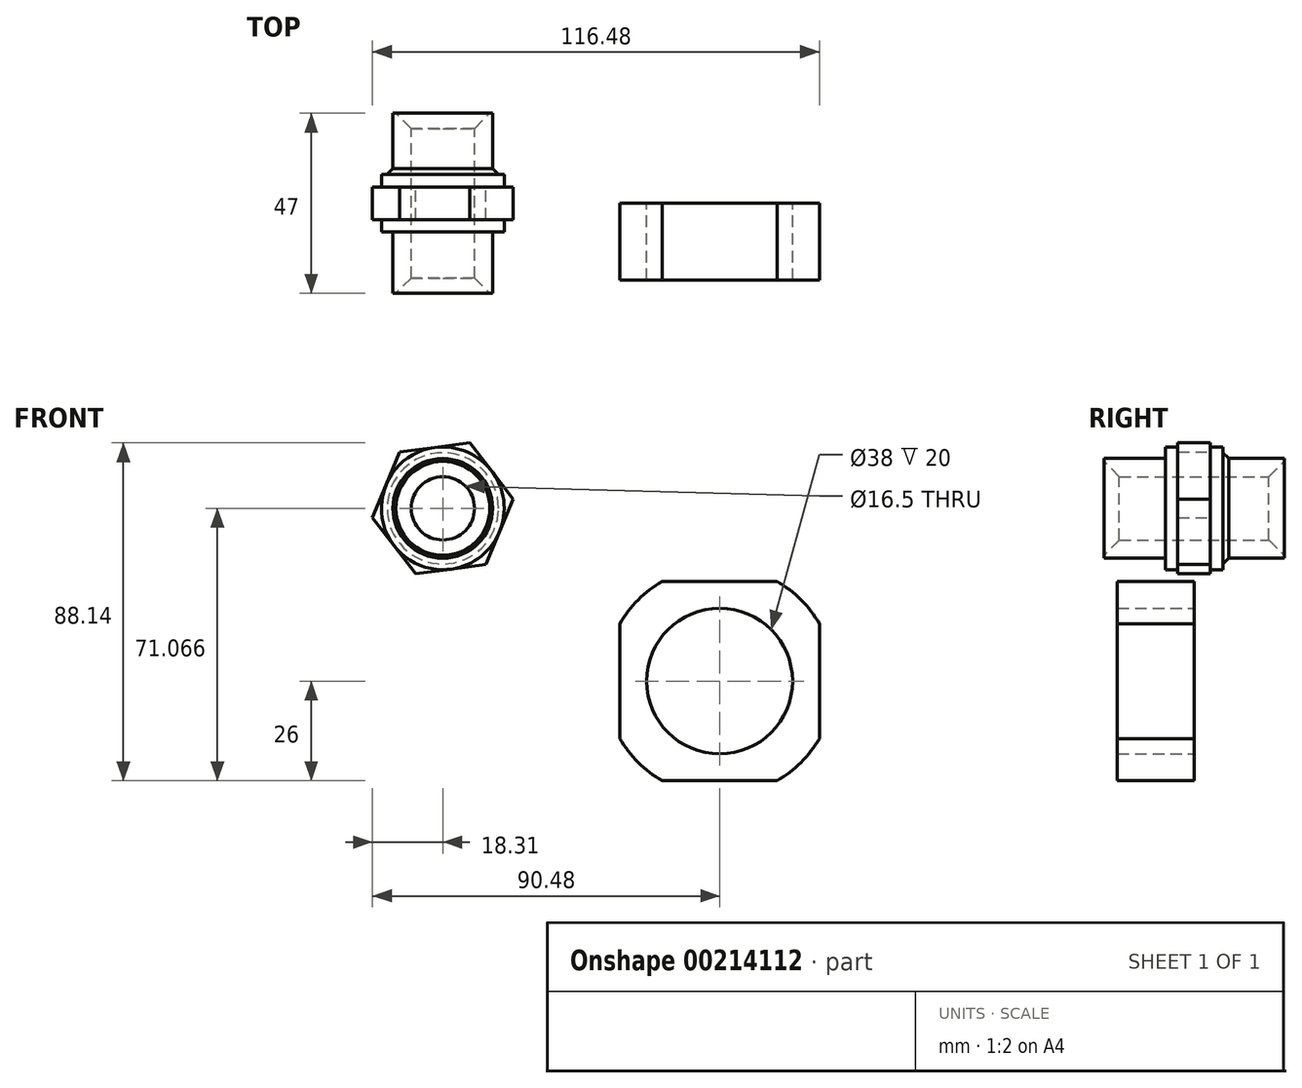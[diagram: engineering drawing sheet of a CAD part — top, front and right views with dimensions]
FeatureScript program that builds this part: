
annotation { "Feature Type Name" : "Feature", "Feature Type Description" : "" }
export const myFeature = defineFeature(function(context is Context, id is Id, definition is map)
    precondition{}
    {
        {
            var Q0;
            Q0=qCreatedBy(makeId("Front.planeOp"),FACE);
            var sketch = newSketch(context, id + "F0", { "sketchPlane" : qUnion([Q0])});
            skLineSegment(sketch, "E0.bottom", {"start": v(26, 26) * mm, "end": v(-26, 26) * mm});
            skLineSegment(sketch, "E0.top", {"start": v(26, -26) * mm, "end": v(-26, -26) * mm});
            skLineSegment(sketch, "E0.left", {"start": v(26, 26) * mm, "end": v(26, -26) * mm});
            skLineSegment(sketch, "E0.right", {"start": v(-26, 26) * mm, "end": v(-26, -26) * mm});
            skPoint(sketch, "E0.middle", {"position": v(0, 0) * mm});
            skCircle(sketch, "E1", {"center": v(0, 0) * mm, "radius": 15 * mm});
            skCircle(sketch, "E2", {"center": v(0, 0) * mm, "radius": 30 * mm});
            skSolve(sketch);
        }
        {
            var Q0;
            Q0=makeQuery(id+"F0.imprint","IMPRINT",FACE,{"disambiguationData":[TD([[makeQuery(id+"F0.imprint","IMPRINT",EDGE,{"derivedFrom":sQuery(id+"F0.wireOp",EDGE,"E1")}),-1.0]])]});
            var Q1;
            Q1=makeQuery(id+"F0.imprint","IMPRINT",FACE,{"disambiguationData":[TD([[makeQuery(id+"F0.imprint","IMPRINT",EDGE,{"derivedFrom":sQuery(id+"F0.wireOp",EDGE,"E1")}),1.0]])]});
            extrude(context, id + "F1", {"entities" : qUnion([Q0, Q1]), "depth" : 20 * mm});
        }
        {
            var Q0;
            Q0=sQuery(id+"F0.wireOp",VERTEX,"E0.middle");
            var Q1;
            Q1=makeQuery(id+"F1.opExtrude","SWEPT_BODY",BODY,{"disambiguationData":[OSD([sQuery(id+"F0.wireOp",EDGE,"E0.bottom"),sQuery(id+"F0.wireOp",EDGE,"E0.top"),sQuery(id+"F0.wireOp",EDGE,"E0.left"),sQuery(id+"F0.wireOp",EDGE,"E0.right"),sQuery(id+"F0.wireOp",EDGE,"E2")])]});
            hole(context, id + "F2", {"style" : HoleStyle.SIMPLE, "endStyle" : HoleEndStyle.BLIND, "oppositeDirection" : true, "standardTappedOrClearance" : lookupTablePath({ "standard" : "ISO", "size" : "38", "type" : "Drilled" }), "standardBlindInLast" : lookupTablePath({ "standard" : "ISO", "size" : "38", "type" : "Drilled" }), "holeDiameter" : 38 * mm, "holeDepth" : 20 * mm, "startFromSketch" : true, "locations" : qUnion([Q0]), "scope" : qUnion([Q1])});
        }
        {
            var Q0;
            Q0=qCreatedBy(makeId("Front.planeOp"),FACE);
            var sketch = newSketch(context, id + "F3", { "sketchPlane" : qUnion([Q0])});
            skCircle(sketch, "E3.cCircle", {"center": v(-72.17, 45.07) * mm, "radius": 16 * mm, "construction": true});
            skLineSegment(sketch, "E3.0", {"start": v(-53.86, 47.5) * mm, "end": v(-60.9, 30.42) * mm});
            skLineSegment(sketch, "E3.1", {"start": v(-60.9, 30.42) * mm, "end": v(-79.22, 28) * mm});
            skLineSegment(sketch, "E3.2", {"start": v(-79.22, 28) * mm, "end": v(-90.48, 42.64) * mm});
            skLineSegment(sketch, "E3.3", {"start": v(-90.48, 42.64) * mm, "end": v(-83.43, 59.71) * mm});
            skLineSegment(sketch, "E3.4", {"start": v(-83.43, 59.71) * mm, "end": v(-65.12, 62.14) * mm});
            skLineSegment(sketch, "E3.5", {"start": v(-65.12, 62.14) * mm, "end": v(-53.86, 47.5) * mm});
            skPoint(sketch, "E3.0.midPoint", {"position": v(-57.38, 38.96) * mm});
            skCircle(sketch, "E4", {"center": v(-72.17, 45.07) * mm, "radius": 16 * mm});
            skCircle(sketch, "E5", {"center": v(-72.17, 45.07) * mm, "radius": 13 * mm});
            skCircle(sketch, "E6", {"center": v(-72.17, 45.07) * mm, "radius": 8.25 * mm});
            skSolve(sketch);
        }
        {
            var Q0;
            Q0=makeQuery(id+"F3.imprint","IMPRINT",FACE,{"disambiguationData":[TD([[makeQuery(id+"F3.imprint","IMPRINT",EDGE,{"derivedFrom":sQuery(id+"F3.wireOp",EDGE,"E5")}),1.0]])]});
            extrude(context, id + "F4", {"entities" : qUnion([Q0]), "endBound" : BoundingType.SYMMETRIC, "depth" : 47 * mm});
        }
        {
            var Q0;
            Q0=makeQuery(id+"F3.imprint","IMPRINT",FACE,{"disambiguationData":[TD([[makeQuery(id+"F3.imprint","IMPRINT",EDGE,{"derivedFrom":sQuery(id+"F3.wireOp",EDGE,"E5")}),-1.0]])]});
            extrude(context, id + "F5", {"entities" : qUnion([Q0]), "operationType" : NewBodyOperationType.ADD, "endBound" : BoundingType.SYMMETRIC, "depth" : (30 / 2) * mm});
        }
        {
            var Q0;
            {var subQ0=sQuery(id+"F3.wireOp",EDGE,"E3.1");var subQ1=sQuery(id+"F3.wireOp",EDGE,"E3.0");var subQ2=makeQuery(id+"F3.imprint","INTERSECT",VERTEX,{"derivedFrom":[subQ1,subQ0]});Q0=makeQuery(id+"F3.imprint","IMPRINT",FACE,{"disambiguationData":[TD([[makeQuery(id+"F3.imprint","IMPRINT",EDGE,{"disambiguationData":[TD([[subQ2,1.0]])],"derivedFrom":subQ1}),-1.0]])]});}
            var Q1;
            {var subQ0=sQuery(id+"F3.wireOp",EDGE,"E3.2");var subQ1=sQuery(id+"F3.wireOp",EDGE,"E3.1");var subQ2=makeQuery(id+"F3.imprint","INTERSECT",VERTEX,{"derivedFrom":[subQ1,subQ0]});Q1=makeQuery(id+"F3.imprint","IMPRINT",FACE,{"disambiguationData":[TD([[makeQuery(id+"F3.imprint","IMPRINT",EDGE,{"disambiguationData":[TD([[subQ2,1.0]])],"derivedFrom":subQ1}),-1.0]])]});}
            var Q2;
            {var subQ0=sQuery(id+"F3.wireOp",EDGE,"E3.3");var subQ1=sQuery(id+"F3.wireOp",EDGE,"E3.2");var subQ2=makeQuery(id+"F3.imprint","INTERSECT",VERTEX,{"derivedFrom":[subQ1,subQ0]});Q2=makeQuery(id+"F3.imprint","IMPRINT",FACE,{"disambiguationData":[TD([[makeQuery(id+"F3.imprint","IMPRINT",EDGE,{"disambiguationData":[TD([[subQ2,1.0]])],"derivedFrom":subQ1}),-1.0]])]});}
            var Q3;
            {var subQ0=sQuery(id+"F3.wireOp",EDGE,"E3.4");var subQ1=sQuery(id+"F3.wireOp",EDGE,"E3.3");var subQ2=makeQuery(id+"F3.imprint","INTERSECT",VERTEX,{"derivedFrom":[subQ1,subQ0]});Q3=makeQuery(id+"F3.imprint","IMPRINT",FACE,{"disambiguationData":[TD([[makeQuery(id+"F3.imprint","IMPRINT",EDGE,{"disambiguationData":[TD([[subQ2,1.0]])],"derivedFrom":subQ1}),-1.0]])]});}
            var Q4;
            {var subQ0=sQuery(id+"F3.wireOp",EDGE,"E3.5");var subQ1=sQuery(id+"F3.wireOp",EDGE,"E3.4");var subQ2=makeQuery(id+"F3.imprint","INTERSECT",VERTEX,{"derivedFrom":[subQ1,subQ0]});Q4=makeQuery(id+"F3.imprint","IMPRINT",FACE,{"disambiguationData":[TD([[makeQuery(id+"F3.imprint","IMPRINT",EDGE,{"disambiguationData":[TD([[subQ2,1.0]])],"derivedFrom":subQ1}),-1.0]])]});}
            var Q5;
            {var subQ0=sQuery(id+"F3.wireOp",EDGE,"E3.5");var subQ1=sQuery(id+"F3.wireOp",EDGE,"E3.0");var subQ2=makeQuery(id+"F3.imprint","INTERSECT",VERTEX,{"derivedFrom":[subQ1,subQ0]});Q5=makeQuery(id+"F3.imprint","IMPRINT",FACE,{"disambiguationData":[TD([[makeQuery(id+"F3.imprint","IMPRINT",EDGE,{"disambiguationData":[TD([[subQ2,-1.0]])],"derivedFrom":subQ1}),-1.0]])]});}
            var Q6;
            Q6=makeQuery(id+"F3.imprint","IMPRINT",FACE,{"disambiguationData":[TD([[makeQuery(id+"F3.imprint","IMPRINT",EDGE,{"derivedFrom":sQuery(id+"F3.wireOp",EDGE,"E4")}),-1.0]])]});
            extrude(context, id + "F6", {"entities" : qUnion([Q0, Q1, Q2, Q3, Q4, Q5, Q6]), "operationType" : NewBodyOperationType.ADD, "endBound" : BoundingType.SYMMETRIC, "depth" : (4.25 * 2) * mm});
        }
        {
            var Q0;
            Q0=makeQuery(id+"F4.opExtrude","CAP_EDGE",EDGE,{"disambiguationData":[OSD([sQuery(id+"F3.wireOp",EDGE,"E6")])],"isStart":false});
            chamfer(context, id + "F7", {"entities" : qUnion([Q0]), "width" : 4 * mm, "tangentPropagation" : true});
        }
        {
            var Q0;
            Q0=makeQuery(id+"F4.opExtrude","CAP_EDGE",EDGE,{"disambiguationData":[OSD([sQuery(id+"F3.wireOp",EDGE,"E6")])],"isStart":true});
            chamfer(context, id + "F8", {"entities" : qUnion([Q0]), "width" : 4 * mm, "tangentPropagation" : true});
        }
        {
            var Q0;
            Q0=makeQuery(id+"F5.opExtrude","CAP_EDGE",EDGE,{"disambiguationData":[OSD([sQuery(id+"F3.wireOp",EDGE,"E5")])],"isStart":true});
            var Q1;
            Q1=makeQuery(id+"F5.opExtrude","CAP_EDGE",EDGE,{"disambiguationData":[OSD([sQuery(id+"F3.wireOp",EDGE,"E5")])],"isStart":false});
            chamfer(context, id + "F9", {"entities" : qUnion([Q0, Q1]), "width" : 1.5 * mm, "tangentPropagation" : true});
        }
    });
